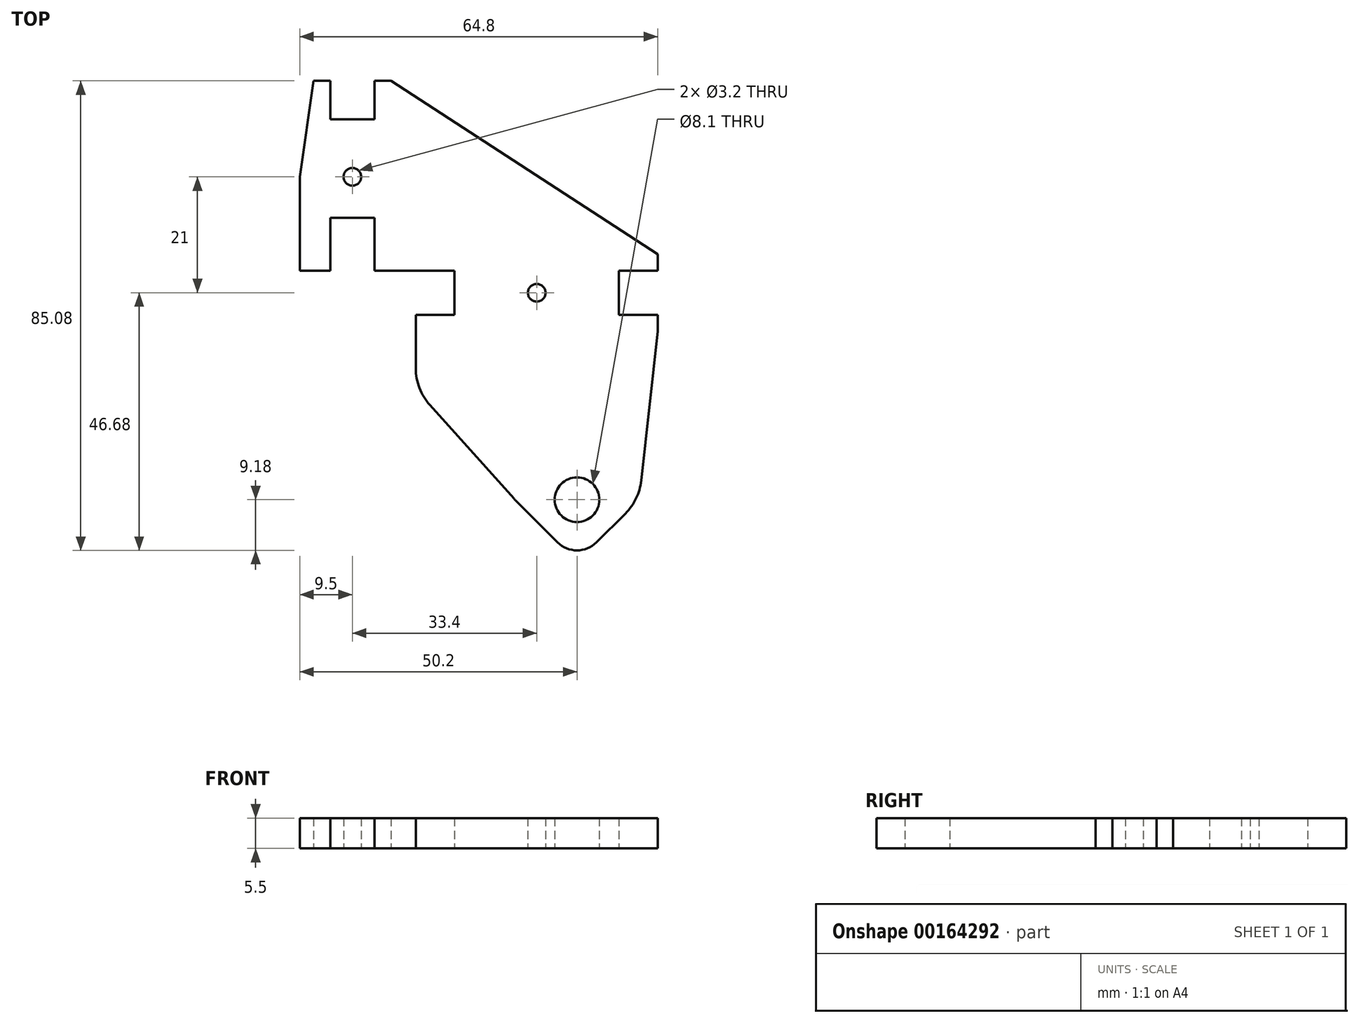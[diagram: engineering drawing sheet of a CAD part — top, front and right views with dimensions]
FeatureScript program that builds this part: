
annotation { "Feature Type Name" : "Feature", "Feature Type Description" : "" }
export const myFeature = defineFeature(function(context is Context, id is Id, definition is map)
    precondition{}
    {
        {
            var Q0;
            Q0=qCreatedBy(makeId("Top.planeOp"),FACE);
            var sketch = newSketch(context, id + "F0", { "sketchPlane" : qUnion([Q0])});
            skCircle(sketch, "E0", {"center": v(0, 0) * mm, "radius": 4.05 * mm});
            skLineSegment(sketch, "E1", {"start": v(0, 0) * mm, "end": v(0, 37.5) * mm, "construction": true});
            skLineSegment(sketch, "E2", {"start": v(0, 37.5) * mm, "end": v(-7.3, 37.5) * mm, "construction": true});
            skCircle(sketch, "E3", {"center": v(-7.3, 37.5) * mm, "radius": 1.6 * mm});
            skLineSegment(sketch, "E4", {"start": v(-7.3, 37.5) * mm, "end": v(-40.7, 37.5) * mm, "construction": true});
            skLineSegment(sketch, "E5", {"start": v(-40.7, 37.5) * mm, "end": v(-40.7, 58.5) * mm, "construction": true});
            skCircle(sketch, "E6", {"center": v(-40.7, 58.5) * mm, "radius": 1.6 * mm});
            skLineSegment(sketch, "E7", {"start": v(-7.3, 37.5) * mm, "end": v(-22.2, 37.5) * mm, "construction": true});
            skLineSegment(sketch, "E8", {"start": v(-7.3, 37.5) * mm, "end": v(7.6, 37.5) * mm, "construction": true});
            skLineSegment(sketch, "E9", {"start": v(-22.2, 37.5) * mm, "end": v(-22.2, 33.5) * mm});
            skLineSegment(sketch, "E10", {"start": v(-22.2, 37.5) * mm, "end": v(-22.2, 41.5) * mm});
            skLineSegment(sketch, "E11", {"start": v(-40.7, 58.5) * mm, "end": v(-50.2, 58.5) * mm, "construction": true});
            skLineSegment(sketch, "E12", {"start": v(-50.2, 58.5) * mm, "end": v(-50.2, 41.5) * mm});
            skLineSegment(sketch, "E13", {"start": v(-22.2, 41.5) * mm, "end": v(-36.7, 41.5) * mm});
            skLineSegment(sketch, "E14", {"start": v(-40.7, 58.5) * mm, "end": v(-40.7, 51.1) * mm, "construction": true});
            skLineSegment(sketch, "E15", {"start": v(-40.7, 58.5) * mm, "end": v(-40.7, 68.9) * mm, "construction": true});
            skLineSegment(sketch, "E16", {"start": v(-40.7, 68.9) * mm, "end": v(-44.7, 68.9) * mm});
            skLineSegment(sketch, "E17", {"start": v(-40.7, 68.9) * mm, "end": v(-36.7, 68.9) * mm});
            skLineSegment(sketch, "E18", {"start": v(-44.7, 68.9) * mm, "end": v(-44.7, 75.9) * mm});
            skLineSegment(sketch, "E19", {"start": v(-36.7, 68.9) * mm, "end": v(-36.7, 75.9) * mm});
            skLineSegment(sketch, "E20", {"start": v(7.6, 37.5) * mm, "end": v(7.6, 41.5) * mm});
            skLineSegment(sketch, "E21", {"start": v(7.6, 37.5) * mm, "end": v(7.6, 33.5) * mm});
            skLineSegment(sketch, "E22", {"start": v(7.6, 41.5) * mm, "end": v(14.6, 41.5) * mm});
            skLineSegment(sketch, "E23", {"start": v(7.6, 33.5) * mm, "end": v(14.6, 33.5) * mm});
            skLineSegment(sketch, "E24", {"start": v(-44.7, 75.9) * mm, "end": v(-47.7, 75.9) * mm});
            skLineSegment(sketch, "E25", {"start": v(-36.7, 75.9) * mm, "end": v(-33.7, 75.9) * mm});
            skLineSegment(sketch, "E26", {"start": v(14.6, 41.5) * mm, "end": v(14.6, 44.5) * mm});
            skLineSegment(sketch, "E27", {"start": v(14.6, 33.5) * mm, "end": v(14.6, 30.5) * mm});
            skLineSegment(sketch, "E28", {"start": v(-47.7, 75.9) * mm, "end": v(-50.2, 58.5) * mm});
            skLineSegment(sketch, "E29", {"start": v(-33.7, 75.9) * mm, "end": v(14.6, 44.5) * mm});
            skLineSegment(sketch, "E30", {"start": v(-22.2, 33.5) * mm, "end": v(-29.2, 33.5) * mm});
            skLineSegment(sketch, "E31", {"start": v(-29.2, 33.5) * mm, "end": v(-29.2, 23.83) * mm});
            skLineSegment(sketch, "E32", {"start": v(0, 0) * mm, "end": v(-11.25, 0) * mm, "construction": true});
            skLineSegment(sketch, "E33", {"start": v(0, 0) * mm, "end": v(0, -11.25) * mm, "construction": true});
            skLineSegment(sketch, "E34", {"start": v(0, 0) * mm, "end": v(11.25, 0) * mm, "construction": true});
            skLineSegment(sketch, "E35", {"start": v(-26.64, 17.15) * mm, "end": v(-11.43, 0.2) * mm});
            skLineSegment(sketch, "E36", {"start": v(-11.06, -0.2) * mm, "end": v(-3.54, -7.71) * mm});
            skLineSegment(sketch, "E37", {"start": v(3.54, -7.71) * mm, "end": v(8.76, -2.49) * mm});
            skLineSegment(sketch, "E38", {"start": v(11.63, 3.5) * mm, "end": v(14.6, 30.5) * mm});
            skPoint(sketch, "E39.visualSharp", {"position": v(-11.25, 0) * mm});
            skArc(sketch, "E39.filletArc", {"start": v(-11.43, 0.2) * mm, "mid": v(-11.12, -0.13) * mm, "end": v(-10.78, -0.45) * mm});
            skArc(sketch, "E40.filletArc", {"start": v(-11.43, 0.2) * mm, "mid": v(-11.25, 0) * mm, "end": v(-11.06, -0.2) * mm});
            skPoint(sketch, "E41.visualSharp", {"position": v(0, -11.25) * mm});
            skArc(sketch, "E41.filletArc", {"start": v(-3.54, -7.71) * mm, "mid": v(0, -9.18) * mm, "end": v(3.54, -7.71) * mm});
            skPoint(sketch, "E42.visualSharp", {"position": v(11.25, 0) * mm});
            skArc(sketch, "E42.filletArc", {"start": v(8.76, -2.49) * mm, "mid": v(10.7, 0.26) * mm, "end": v(11.63, 3.5) * mm});
            skPoint(sketch, "E43.visualSharp", {"position": v(-29.2, 20) * mm});
            skArc(sketch, "E43.filletArc", {"start": v(-29.2, 23.83) * mm, "mid": v(-28.54, 20.25) * mm, "end": v(-26.64, 17.15) * mm});
            skLineSegment(sketch, "E44", {"start": v(-40.7, 51.1) * mm, "end": v(-44.7, 51.1) * mm});
            skLineSegment(sketch, "E45", {"start": v(-40.7, 51.1) * mm, "end": v(-36.7, 51.1) * mm});
            skLineSegment(sketch, "E46", {"start": v(-44.7, 51.1) * mm, "end": v(-44.7, 41.5) * mm});
            skLineSegment(sketch, "E47", {"start": v(-36.7, 51.1) * mm, "end": v(-36.7, 41.5) * mm});
            skLineSegment(sketch, "E48.trimOffspring", {"start": v(-44.7, 41.5) * mm, "end": v(-50.2, 41.5) * mm});
            skSolve(sketch);
        }
        {
            var Q0;
            Q0=makeQuery(id+"F0.imprint","IMPRINT",FACE,{"disambiguationData":[TD([[makeQuery(id+"F0.imprint","IMPRINT",EDGE,{"derivedFrom":sQuery(id+"F0.wireOp",EDGE,"E0")}),-1.0]])]});
            extrude(context, id + "F1", {"entities" : qUnion([Q0]), "depth" : 5.5 * mm});
        }
    });
